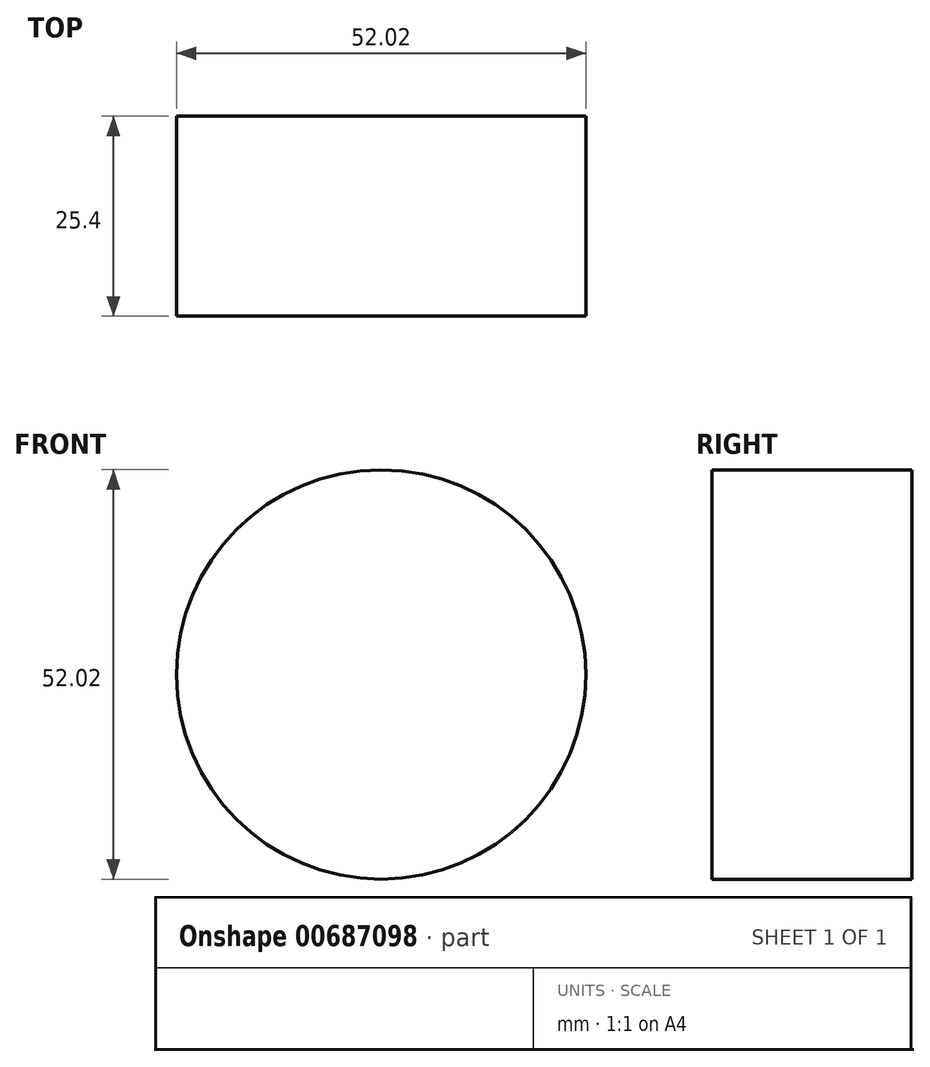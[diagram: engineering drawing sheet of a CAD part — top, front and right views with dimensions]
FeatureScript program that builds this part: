
annotation { "Feature Type Name" : "Feature", "Feature Type Description" : "" }
export const myFeature = defineFeature(function(context is Context, id is Id, definition is map)
    precondition{}
    {
        {
            var Q0;
            Q0=qCreatedBy(makeId("Front.planeOp"),FACE);
            var sketch = newSketch(context, id + "F0", { "sketchPlane" : qUnion([Q0])});
            skCircle(sketch, "E0", {"center": v(0, 0) * mm, "radius": 26 * mm});
            skSolve(sketch);
        }
        {
            var Q0;
            Q0 = qSketchRegion(id + "F0", true);
            extrude(context, id + "F1", {"entities" : qUnion([Q0]), "depth" : 25.4 * mm, "offsetDistance" : 25.4 * mm});
        }
    });
